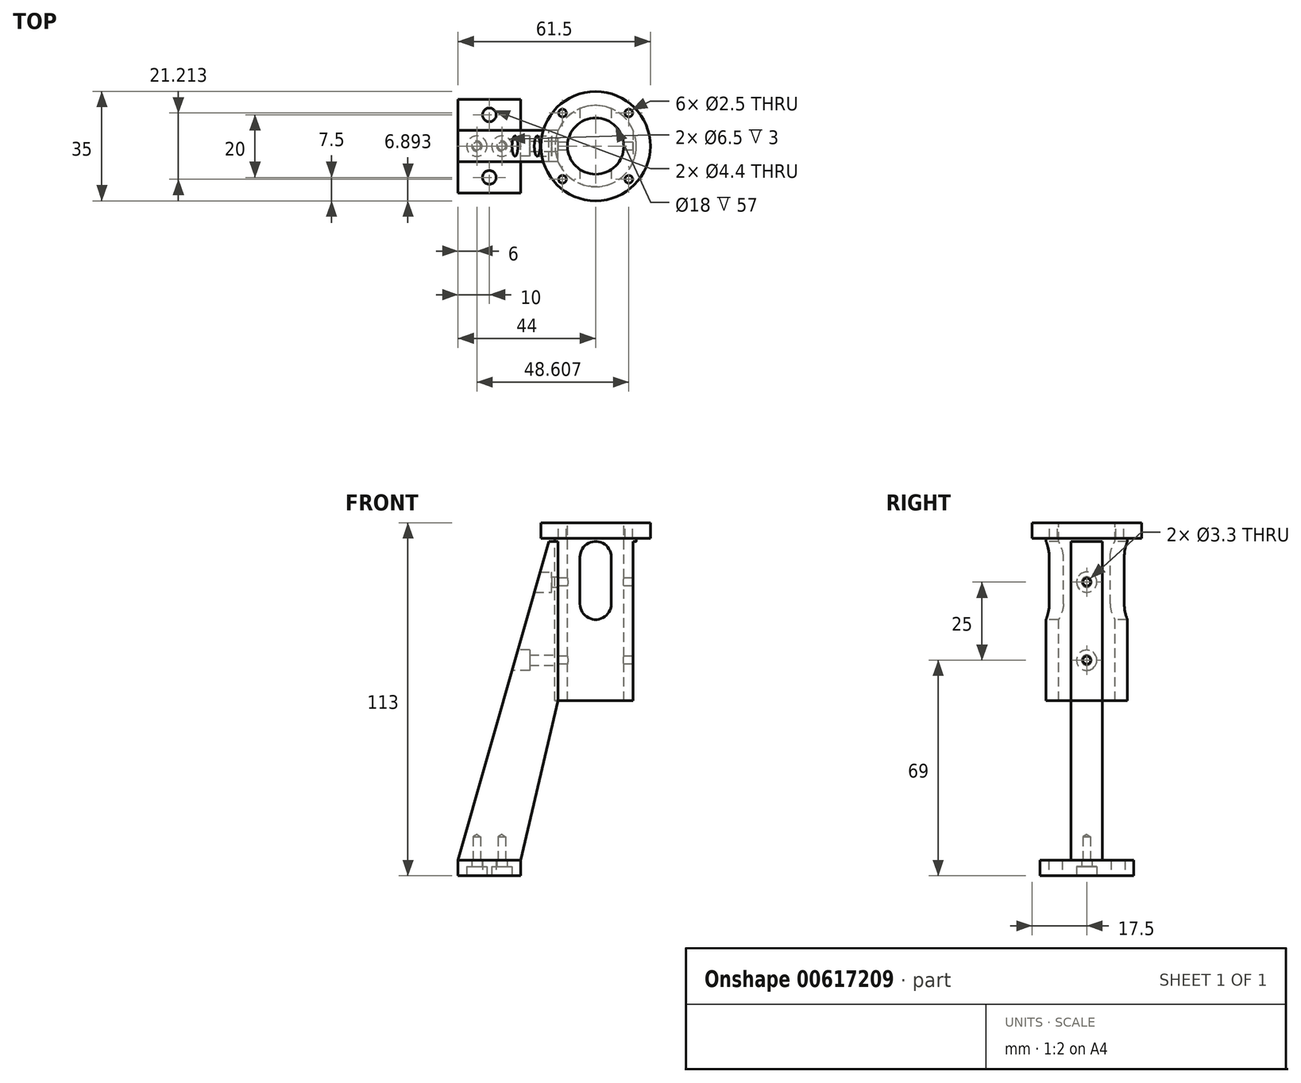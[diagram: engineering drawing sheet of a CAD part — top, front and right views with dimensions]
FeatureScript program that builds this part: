
annotation { "Feature Type Name" : "Feature", "Feature Type Description" : "" }
export const myFeature = defineFeature(function(context is Context, id is Id, definition is map)
    precondition{}
    {
        {
            var Q0;
            Q0=qCreatedBy(makeId("Front.planeOp"),FACE);
            var sketch = newSketch(context, id + "F0", { "sketchPlane" : qUnion([Q0])});
            skLineSegment(sketch, "E0", {"start": v(0, 0) * mm, "end": v(0, -44.79) * mm, "construction": true});
            skLineSegment(sketch, "E1", {"start": v(9, 0) * mm, "end": v(17.5, 0) * mm});
            skLineSegment(sketch, "E2", {"start": v(9, 0) * mm, "end": v(9, -57) * mm});
            skLineSegment(sketch, "E3", {"start": v(17.5, 0) * mm, "end": v(17.5, -5) * mm});
            skLineSegment(sketch, "E4", {"start": v(17.5, -5) * mm, "end": v(13, -5) * mm});
            skLineSegment(sketch, "E5", {"start": v(13, -5) * mm, "end": v(13, -57) * mm});
            skLineSegment(sketch, "E6", {"start": v(13, -57) * mm, "end": v(9, -57) * mm});
            skSolve(sketch);
        }
        {
            var Q0;
            Q0 = qSketchRegion(id + "F0", true);
            var Q1;
            Q1=sQuery(id+"F0.wireOp",EDGE,"E0");
            revolve(context, id + "F1", {"entities" : qUnion([Q0]), "axis" : qUnion([Q1]), "revolveType" : RevolveType.FULL});
        }
        {
            var Q0;
            Q0=qCreatedBy(makeId("Front.planeOp"),FACE);
            var sketch = newSketch(context, id + "F2", { "sketchPlane" : qUnion([Q0])});
            skLineSegment(sketch, "E7.bottom", {"start": v(17.5, -6) * mm, "end": v(12, -6) * mm});
            skLineSegment(sketch, "E7.top", {"start": v(17.5, -57) * mm, "end": v(12, -57) * mm});
            skLineSegment(sketch, "E7.left", {"start": v(17.5, -6) * mm, "end": v(17.5, -57) * mm});
            skLineSegment(sketch, "E7.right", {"start": v(12, -6) * mm, "end": v(12, -57) * mm});
            skSolve(sketch);
        }
        {
            var Q0;
            Q0 = qSketchRegion(id + "F2", true);
            extrude(context, id + "F3", {"entities" : qUnion([Q0]), "operationType" : NewBodyOperationType.REMOVE, "endBound" : BoundingType.THROUGH_ALL, "oppositeDirection" : true, "depth" : 25 * mm, "offsetDistance" : 25 * mm, "hasSecondDirection" : true, "secondDirectionBound" : SecondDirectionBoundingType.THROUGH_ALL, "secondDirectionOppositeDirection" : false, "secondDirectionDepth" : 25 * mm});
        }
        {
            var Q0;
            Q0=qCreatedBy(makeId("Front.planeOp"),FACE);
            var sketch = newSketch(context, id + "F4", { "sketchPlane" : qUnion([Q0])});
            skLineSegment(sketch, "E8", {"start": v(0, -11) * mm, "end": v(0, -26) * mm, "construction": true});
            skArc(sketch, "E9.0.startCap", {"start": v(-5, -11) * mm, "mid": v(0, -6) * mm, "end": v(5, -11) * mm});
            skArc(sketch, "E9.0.endCap", {"start": v(5, -26) * mm, "mid": v(0, -31) * mm, "end": v(-5, -26) * mm});
            skLineSegment(sketch, "E9.0.left", {"start": v(5, -11) * mm, "end": v(5, -26) * mm});
            skLineSegment(sketch, "E9.0.right", {"start": v(-5, -11) * mm, "end": v(-5, -26) * mm});
            skSolve(sketch);
        }
        {
            var Q0;
            Q0 = qSketchRegion(id + "F4", true);
            extrude(context, id + "F5", {"entities" : qUnion([Q0]), "operationType" : NewBodyOperationType.REMOVE, "endBound" : BoundingType.THROUGH_ALL, "oppositeDirection" : true, "depth" : 25 * mm, "offsetDistance" : 25 * mm, "hasSecondDirection" : true, "secondDirectionBound" : SecondDirectionBoundingType.THROUGH_ALL, "secondDirectionOppositeDirection" : false, "secondDirectionDepth" : 25 * mm});
        }
        {
            var Q0;
            Q0=makeQuery(id+"F1.opRevolve","SWEPT_FACE",FACE,{"disambiguationData":[OSD([sQuery(id+"F0.wireOp",EDGE,"E1")])]});
            var sketch = newSketch(context, id + "F6", { "sketchPlane" : qUnion([Q0])});
            skCircle(sketch, "E10", {"center": v(0, 0) * mm, "radius": 15 * mm, "construction": true});
            skLineSegment(sketch, "E11", {"start": v(-10.6, -10.6) * mm, "end": v(10.6, 10.6) * mm, "construction": true});
            skLineSegment(sketch, "E12", {"start": v(-10.6, 10.6) * mm, "end": v(10.6, -10.6) * mm, "construction": true});
            skSolve(sketch);
        }
        {
            var Q0;
            Q0=sQuery(id+"F6.wireOp",VERTEX,"E11.end");
            var Q1;
            Q1=sQuery(id+"F6.wireOp",VERTEX,"E12.start");
            var Q2;
            Q2=sQuery(id+"F6.wireOp",VERTEX,"E11.start");
            var Q3;
            Q3=sQuery(id+"F6.wireOp",VERTEX,"E12.end");
            var Q4;
            Q4=makeQuery(id+"F1.opRevolve","SWEPT_BODY",BODY,{"disambiguationData":[OSD([sQuery(id+"F0.wireOp",EDGE,"E1"),sQuery(id+"F0.wireOp",EDGE,"E2"),sQuery(id+"F0.wireOp",EDGE,"E3"),sQuery(id+"F0.wireOp",EDGE,"E4"),sQuery(id+"F0.wireOp",EDGE,"E5"),sQuery(id+"F0.wireOp",EDGE,"E6")])]});
            hole(context, id + "F7", {"style" : HoleStyle.SIMPLE, "endStyle" : HoleEndStyle.THROUGH, "standardTappedOrClearance" : lookupTablePath({ "standard" : "ISO", "engagement" : "75%", "pitch" : "0.5 mm", "size" : "M3", "type" : "Tapped" }), "standardBlindInLast" : lookupTablePath({ "standard" : "ISO", "engagement" : "75%", "pitch" : "0.5 mm", "size" : "M3", "type" : "Tapped" }), "holeDiameter" : 2.5 * mm, "majorDiameter" : 3 * mm, "showTappedDepth" : true, "isTappedThrough" : true, "tappedDepth" : 12 * mm, "tapClearance" : 3, "locations" : qUnion([Q0, Q1, Q2, Q3]), "scope" : qUnion([Q4])});
        }
        {
            var Q0;
            Q0=qCreatedBy(makeId("Front.planeOp"),FACE);
            var sketch = newSketch(context, id + "F8", { "sketchPlane" : qUnion([Q0])});
            skLineSegment(sketch, "E13", {"start": v(-12, -6) * mm, "end": v(-12, -57) * mm});
            skLineSegment(sketch, "E14", {"start": v(-12, -6) * mm, "end": v(-15, -6) * mm});
            skLineSegment(sketch, "E15", {"start": v(-15, -6) * mm, "end": v(-44, -108) * mm});
            skLineSegment(sketch, "E16", {"start": v(-12, -57) * mm, "end": v(-24, -108) * mm});
            skLineSegment(sketch, "E17", {"start": v(-44, -108) * mm, "end": v(-24, -108) * mm});
            skSolve(sketch);
        }
        {
            var Q0;
            Q0 = qSketchRegion(id + "F8", true);
            extrude(context, id + "F9", {"entities" : qUnion([Q0]), "endBound" : BoundingType.SYMMETRIC, "depth" : 10 * mm, "offsetDistance" : 25 * mm});
        }
        {
            var Q0;
            Q0=makeQuery(id+"F9.opExtrude","SWEPT_FACE",FACE,{"disambiguationData":[OSD([sQuery(id+"F8.wireOp",EDGE,"E17")])]});
            var sketch = newSketch(context, id + "F10", { "sketchPlane" : qUnion([Q0])});
            skLineSegment(sketch, "E18.bottom", {"start": v(-24, 15) * mm, "end": v(-44, 15) * mm});
            skLineSegment(sketch, "E18.top", {"start": v(-24, -15) * mm, "end": v(-44, -15) * mm});
            skLineSegment(sketch, "E18.left", {"start": v(-24, 15) * mm, "end": v(-24, -15) * mm});
            skLineSegment(sketch, "E18.right", {"start": v(-44, 15) * mm, "end": v(-44, -15) * mm});
            skPoint(sketch, "E18.middle", {"position": v(-34, 0) * mm});
            skPoint(sketch, "E18.middle.positionSnap0", {"position": v(-34, -5) * mm});
            skPoint(sketch, "E18.centerSnap0", {"position": v(-34, -5) * mm});
            skSolve(sketch);
        }
        {
            var Q0;
            Q0 = qSketchRegion(id + "F10", true);
            extrude(context, id + "F11", {"entities" : qUnion([Q0]), "depth" : 5 * mm, "offsetDistance" : 25 * mm});
        }
        {
            var Q0;
            Q0=makeQuery(id+"F11.opExtrude","CAP_FACE",FACE,{"disambiguationData":[OSD([sQuery(id+"F10.wireOp",EDGE,"E18.bottom"),sQuery(id+"F10.wireOp",EDGE,"E18.top"),sQuery(id+"F10.wireOp",EDGE,"E18.left"),sQuery(id+"F10.wireOp",EDGE,"E18.right")])],"isStart":false});
            var sketch = newSketch(context, id + "F12", { "sketchPlane" : qUnion([Q0])});
            skLineSegment(sketch, "E19", {"start": v(-34, 10) * mm, "end": v(-34, -10) * mm, "construction": true});
            skPoint(sketch, "E19.startSnap0", {"position": v(-34, 15) * mm});
            skLineSegment(sketch, "E20", {"start": v(-44, 0) * mm, "end": v(-24, 0) * mm, "construction": true});
            skPoint(sketch, "E21", {"position": v(-30, 0) * mm});
            skPoint(sketch, "E22", {"position": v(-38, 0) * mm});
            skSolve(sketch);
        }
        {
            var Q0;
            Q0=sQuery(id+"F12.wireOp",VERTEX,"E22");
            var Q1;
            Q1=sQuery(id+"F12.wireOp",VERTEX,"E21");
            var Q2;
            Q2=makeQuery(id+"F11.opExtrude","SWEPT_BODY",BODY,{"disambiguationData":[OSD([sQuery(id+"F10.wireOp",EDGE,"E18.bottom"),sQuery(id+"F10.wireOp",EDGE,"E18.top"),sQuery(id+"F10.wireOp",EDGE,"E18.left"),sQuery(id+"F10.wireOp",EDGE,"E18.right")])]});
            hole(context, id + "F13", {"style" : HoleStyle.C_BORE, "endStyle" : HoleEndStyle.THROUGH, "standardTappedOrClearance" : lookupTablePath({ "standard" : "ISO", "fit" : "Normal", "size" : "M3", "type" : "Clearance" }), "standardBlindInLast" : lookupTablePath({ "fit" : "Standard", "standard" : "ISO", "size" : "M3", "type" : "Clearance" }), "holeDiameter" : 3.3 * mm, "cBoreDiameter" : 6.5 * mm, "cBoreDepth" : 3 * mm, "majorDiameter" : 3 * mm, "isTappedThrough" : true, "tappedDepth" : 12 * mm, "tapClearance" : 3, "locations" : qUnion([Q0, Q1]), "scope" : qUnion([Q2])});
        }
        {
            var Q0;
            Q0=sQuery(id+"F12.wireOp",VERTEX,"E22");
            var Q1;
            Q1=sQuery(id+"F12.wireOp",VERTEX,"E21");
            var Q2;
            Q2=makeQuery(id+"F9.opExtrude","SWEPT_BODY",BODY,{"disambiguationData":[OSD([sQuery(id+"F8.wireOp",EDGE,"E13"),sQuery(id+"F8.wireOp",EDGE,"E14"),sQuery(id+"F8.wireOp",EDGE,"E15"),sQuery(id+"F8.wireOp",EDGE,"E16"),sQuery(id+"F8.wireOp",EDGE,"E17")])]});
            hole(context, id + "F14", {"style" : HoleStyle.SIMPLE, "endStyle" : HoleEndStyle.BLIND, "standardTappedOrClearance" : lookupTablePath({ "standard" : "ISO", "engagement" : "75%", "pitch" : "0.5 mm", "size" : "M3", "type" : "Tapped" }), "standardBlindInLast" : lookupTablePath({ "standard" : "ISO", "engagement" : "75%", "pitch" : "0.5 mm", "size" : "M3", "type" : "Tapped" }), "holeDiameter" : 2.5 * mm, "majorDiameter" : 3 * mm, "showTappedDepth" : true, "holeDepth" : 7.5 * mm, "tappedDepth" : 6 * mm, "tapClearance" : 3, "locations" : qUnion([Q0, Q1]), "scope" : qUnion([Q2])});
        }
        {
            var Q0;
            Q0=sQuery(id+"F12.wireOp",VERTEX,"E19.start");
            var Q1;
            Q1=sQuery(id+"F12.wireOp",VERTEX,"E19.end");
            var Q2;
            Q2=makeQuery(id+"F11.opExtrude","SWEPT_BODY",BODY,{"disambiguationData":[OSD([sQuery(id+"F10.wireOp",EDGE,"E18.bottom"),sQuery(id+"F10.wireOp",EDGE,"E18.top"),sQuery(id+"F10.wireOp",EDGE,"E18.left"),sQuery(id+"F10.wireOp",EDGE,"E18.right")])]});
            hole(context, id + "F15", {"style" : HoleStyle.SIMPLE, "endStyle" : HoleEndStyle.THROUGH, "standardTappedOrClearance" : lookupTablePath({ "standard" : "ISO", "fit" : "Normal", "size" : "M4", "type" : "Clearance" }), "standardBlindInLast" : lookupTablePath({ "fit" : "Standard", "standard" : "ISO", "size" : "M4", "type" : "Clearance" }), "holeDiameter" : 4.4 * mm, "majorDiameter" : 3 * mm, "tappedDepth" : 6 * mm, "tapClearance" : 3, "locations" : qUnion([Q0, Q1]), "scope" : qUnion([Q2])});
        }
        {
            var Q0;
            Q0=makeQuery(id+"F9.opExtrude","SWEPT_FACE",FACE,{"disambiguationData":[OSD([sQuery(id+"F8.wireOp",EDGE,"E13")])]});
            var sketch = newSketch(context, id + "F16", { "sketchPlane" : qUnion([Q0])});
            skLineSegment(sketch, "E23", {"start": v(0, -19) * mm, "end": v(0, -44) * mm, "construction": true});
            skSolve(sketch);
        }
        {
            var Q0;
            Q0=sQuery(id+"F16.wireOp",VERTEX,"E23.start");
            var Q1;
            Q1=sQuery(id+"F16.wireOp",VERTEX,"E23.end");
            var Q2;
            Q2=makeQuery(id+"F9.opExtrude","SWEPT_BODY",BODY,{"disambiguationData":[OSD([sQuery(id+"F8.wireOp",EDGE,"E13"),sQuery(id+"F8.wireOp",EDGE,"E14"),sQuery(id+"F8.wireOp",EDGE,"E15"),sQuery(id+"F8.wireOp",EDGE,"E16"),sQuery(id+"F8.wireOp",EDGE,"E17")])]});
            hole(context, id + "F17", {"style" : HoleStyle.SIMPLE, "endStyle" : HoleEndStyle.THROUGH, "standardTappedOrClearance" : lookupTablePath({ "standard" : "ISO", "fit" : "Normal", "size" : "M3", "type" : "Clearance" }), "standardBlindInLast" : lookupTablePath({ "fit" : "Standard", "standard" : "ISO", "size" : "M3", "type" : "Clearance" }), "holeDiameter" : 3.3 * mm, "majorDiameter" : 3 * mm, "tappedDepth" : 6 * mm, "tapClearance" : 3, "locations" : qUnion([Q0, Q1]), "scope" : qUnion([Q2])});
        }
        {
            var Q0;
            Q0=qCreatedBy(makeId("Front.planeOp"),FACE);
            var sketch = newSketch(context, id + "F18", { "sketchPlane" : qUnion([Q0])});
            skLineSegment(sketch, "E24", {"start": v(-25.19, -19) * mm, "end": v(-12, -19) * mm, "construction": true});
            skLineSegment(sketch, "E25", {"start": v(-23.17, -19) * mm, "end": v(-23.17, -22.25) * mm});
            skLineSegment(sketch, "E26", {"start": v(-23.17, -22.25) * mm, "end": v(-14.1, -22.25) * mm});
            skLineSegment(sketch, "E27", {"start": v(-14.1, -22.25) * mm, "end": v(-14.1, -19) * mm});
            skLineSegment(sketch, "E28", {"start": v(-14.1, -19) * mm, "end": v(-23.17, -19) * mm});
            skLineSegment(sketch, "E29.0", {"start": v(-19.17, -20.65) * mm, "end": v(-18.23, -17.35) * mm, "construction": true});
            skSolve(sketch);
        }
        {
            var Q0;
            Q0 = qSketchRegion(id + "F18", true);
            var Q1;
            Q1=sQuery(id+"F18.wireOp",EDGE,"E24");
            revolve(context, id + "F19", {"operationType" : NewBodyOperationType.REMOVE, "entities" : qUnion([Q0]), "axis" : qUnion([Q1]), "revolveType" : RevolveType.FULL, "oppositeDirection" : true});
        }
        {
            var Q0;
            Q0=qCreatedBy(makeId("Front.planeOp"),FACE);
            var sketch = newSketch(context, id + "F20", { "sketchPlane" : qUnion([Q0])});
            skLineSegment(sketch, "E30.0", {"start": v(-26.27, -45.65) * mm, "end": v(-25.33, -42.35) * mm, "construction": true});
            skLineSegment(sketch, "E31", {"start": v(-12, -44) * mm, "end": v(-30.14, -44) * mm, "construction": true});
            skLineSegment(sketch, "E32.bottom", {"start": v(-21.1, -44) * mm, "end": v(-30.27, -44) * mm});
            skLineSegment(sketch, "E32.top", {"start": v(-21.1, -47.25) * mm, "end": v(-30.27, -47.25) * mm});
            skLineSegment(sketch, "E32.left", {"start": v(-21.1, -44) * mm, "end": v(-21.1, -47.25) * mm});
            skLineSegment(sketch, "E32.right", {"start": v(-30.27, -44) * mm, "end": v(-30.27, -47.25) * mm});
            skSolve(sketch);
        }
        {
            var Q0;
            Q0 = qSketchRegion(id + "F20", true);
            var Q1;
            Q1=sQuery(id+"F20.wireOp",EDGE,"E31");
            revolve(context, id + "F21", {"operationType" : NewBodyOperationType.REMOVE, "entities" : qUnion([Q0]), "axis" : qUnion([Q1]), "revolveType" : RevolveType.FULL, "oppositeDirection" : true});
        }
        {
            var Q0;
            Q0=sQuery(id+"F16.wireOp",VERTEX,"E23.start");
            var Q1;
            Q1=sQuery(id+"F16.wireOp",VERTEX,"E23.end");
            var Q2;
            Q2=makeQuery(id+"F1.opRevolve","SWEPT_BODY",BODY,{"disambiguationData":[OSD([sQuery(id+"F0.wireOp",EDGE,"E1"),sQuery(id+"F0.wireOp",EDGE,"E2"),sQuery(id+"F0.wireOp",EDGE,"E3"),sQuery(id+"F0.wireOp",EDGE,"E4"),sQuery(id+"F0.wireOp",EDGE,"E5"),sQuery(id+"F0.wireOp",EDGE,"E6")])]});
            hole(context, id + "F22", {"style" : HoleStyle.SIMPLE, "endStyle" : HoleEndStyle.THROUGH, "oppositeDirection" : true, "standardTappedOrClearance" : lookupTablePath({ "standard" : "ISO", "engagement" : "75%", "pitch" : "0.5 mm", "size" : "M3", "type" : "Tapped" }), "standardBlindInLast" : lookupTablePath({ "standard" : "ISO", "engagement" : "75%", "pitch" : "0.5 mm", "size" : "M3", "type" : "Tapped" }), "holeDiameter" : 2.5 * mm, "majorDiameter" : 3 * mm, "showTappedDepth" : true, "isTappedThrough" : true, "tappedDepth" : 6 * mm, "tapClearance" : 3, "locations" : qUnion([Q0, Q1]), "scope" : qUnion([Q2])});
        }
    });
